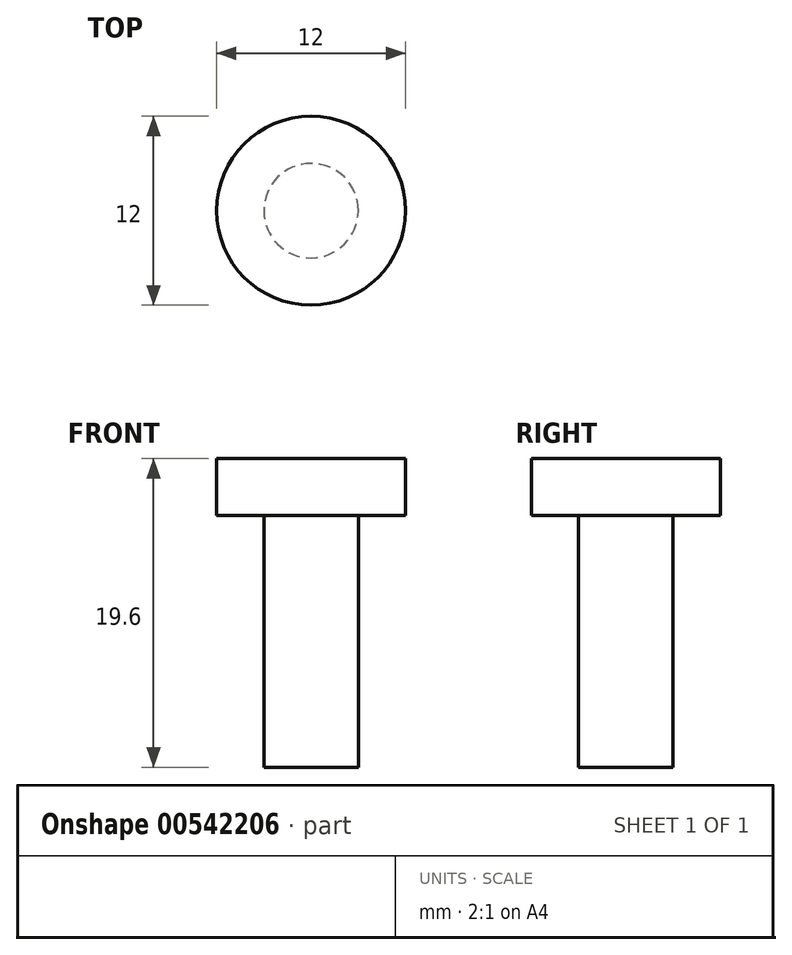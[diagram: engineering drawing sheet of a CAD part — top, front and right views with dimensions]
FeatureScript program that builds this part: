
annotation { "Feature Type Name" : "Feature", "Feature Type Description" : "" }
export const myFeature = defineFeature(function(context is Context, id is Id, definition is map)
    precondition{}
    {
        {
            var Q0;
            Q0=qCreatedBy(makeId("Top.planeOp"),FACE);
            var sketch = newSketch(context, id + "F0", { "sketchPlane" : qUnion([Q0])});
            skCircle(sketch, "E0", {"center": v(0, 0) * mm, "radius": 3 * mm});
            skSolve(sketch);
        }
        {
            var Q0;
            Q0=makeQuery(id+"F0.imprint","IMPRINT",FACE,{"disambiguationData":[TD([[makeQuery(id+"F0.imprint","IMPRINT",EDGE,{"derivedFrom":sQuery(id+"F0.wireOp",EDGE,"E0")}),1.0]])]});
            extrude(context, id + "F1", {"entities" : qUnion([Q0]), "depth" : 16 * mm, "offsetDistance" : 25 * mm});
        }
        {
            var Q0;
            Q0=makeQuery(id+"F1.opExtrude","CAP_FACE",FACE,{"disambiguationData":[OSD([sQuery(id+"F0.wireOp",EDGE,"E0")])],"isStart":false});
            var sketch = newSketch(context, id + "F2", { "sketchPlane" : qUnion([Q0])});
            skCircle(sketch, "E1", {"center": v(0, 0) * mm, "radius": 6 * mm});
            skSolve(sketch);
        }
        {
            var Q0;
            Q0=makeQuery(id+"F2.imprint","IMPRINT",FACE,{"disambiguationData":[TD([[makeQuery(id+"F2.imprint","IMPRINT",EDGE,{"derivedFrom":makeQuery(id+"F1.opExtrude","CAP_EDGE",EDGE,{"disambiguationData":[OSD([sQuery(id+"F0.wireOp",EDGE,"E0")])],"isStart":false})}),1.0]])]});
            var Q1;
            Q1=makeQuery(id+"F2.imprint","IMPRINT",FACE,{"disambiguationData":[TD([[makeQuery(id+"F2.imprint","IMPRINT",EDGE,{"derivedFrom":sQuery(id+"F2.wireOp",EDGE,"E1")}),1.0]])]});
            extrude(context, id + "F3", {"entities" : qUnion([Q0, Q1]), "depth" : 3.6 * mm, "offsetDistance" : 25 * mm});
        }
    });
